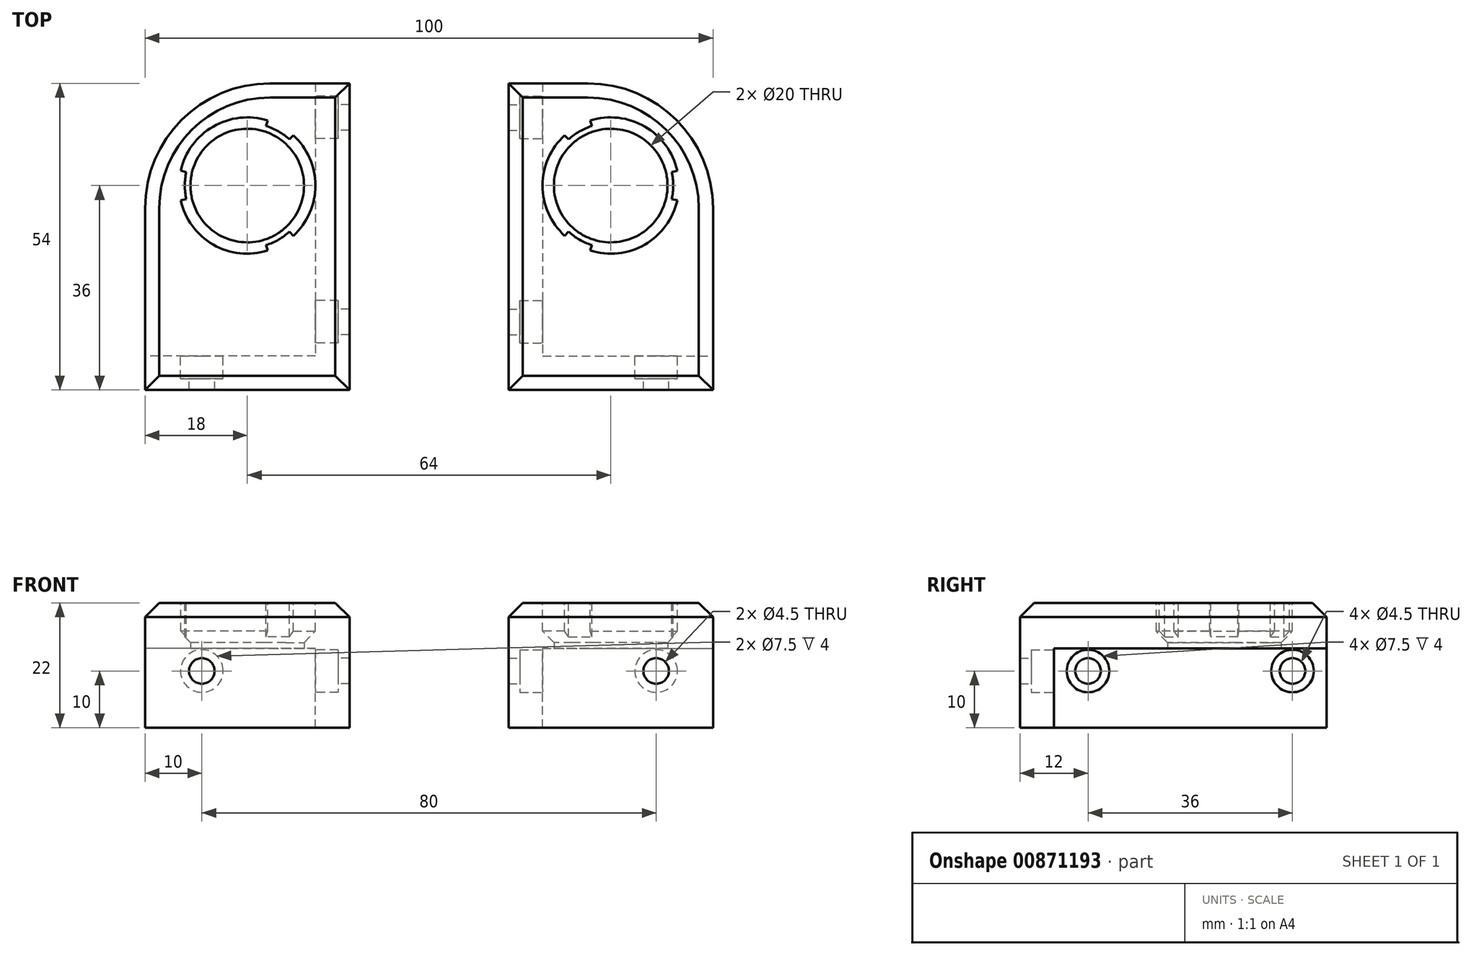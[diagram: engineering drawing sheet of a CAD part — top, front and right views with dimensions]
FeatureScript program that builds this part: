
annotation { "Feature Type Name" : "Feature", "Feature Type Description" : "" }
export const myFeature = defineFeature(function(context is Context, id is Id, definition is map)
    precondition{}
    {
        {
            var Q0;
            Q0=qCreatedBy(makeId("Top.planeOp"),FACE);
            var sketch = newSketch(context, id + "F0", { "sketchPlane" : qUnion([Q0])});
            skLineSegment(sketch, "E0.bottom", {"start": v(0, 0) * mm, "end": v(36, 0) * mm});
            skLineSegment(sketch, "E0.top", {"start": v(0, 54) * mm, "end": v(36, 54) * mm});
            skLineSegment(sketch, "E0.left", {"start": v(0, 0) * mm, "end": v(0, 54) * mm});
            skLineSegment(sketch, "E0.right", {"start": v(36, 0) * mm, "end": v(36, 54) * mm});
            skCircle(sketch, "E1", {"center": v(18, 36) * mm, "radius": 10 * mm});
            skPoint(sketch, "E1.centerSnap0", {"position": v(36, 27) * mm});
            skPoint(sketch, "E1.centerSnap1", {"position": v(18, 54) * mm});
            skSolve(sketch);
        }
        {
            var Q0;
            Q0=qSketchRegion(id+"F0",true);
            extrude(context, id + "F1", {"entities" : qUnion([Q0]), "depth" : 8 * mm, "offsetDistance" : 25 * mm});
        }
        {
            var Q0;
            Q0=makeQuery(id+"F1.opExtrude","CAP_FACE",FACE,{"disambiguationData":[OSD([sQuery(id+"F0.wireOp",EDGE,"E0.bottom"),sQuery(id+"F0.wireOp",EDGE,"E0.top"),sQuery(id+"F0.wireOp",EDGE,"E0.left"),sQuery(id+"F0.wireOp",EDGE,"E0.right"),sQuery(id+"F0.wireOp",EDGE,"E1")])],"isStart":true});
            var sketch = newSketch(context, id + "F2", { "sketchPlane" : qUnion([Q0])});
            skLineSegment(sketch, "E2", {"start": v(0, 0) * mm, "end": v(36, 0) * mm});
            skLineSegment(sketch, "E3", {"start": v(36, 0) * mm, "end": v(36, -54) * mm});
            skLineSegment(sketch, "E4", {"start": v(36, -54) * mm, "end": v(30, -54) * mm});
            skLineSegment(sketch, "E5", {"start": v(30, -54) * mm, "end": v(30, -6) * mm});
            skLineSegment(sketch, "E6", {"start": v(30, -6) * mm, "end": v(0, -6) * mm});
            skLineSegment(sketch, "E7", {"start": v(0, -6) * mm, "end": v(0, 0) * mm});
            skSolve(sketch);
        }
        {
            var Q0;
            Q0=makeQuery(id+"F2.imprint","IMPRINT",FACE,{"disambiguationData":[TD([[makeQuery(id+"F2.imprint","IMPRINT",EDGE,{"derivedFrom":sQuery(id+"F2.wireOp",EDGE,"E2")}),-1.0]])]});
            extrude(context, id + "F3", {"entities" : qUnion([Q0]), "operationType" : NewBodyOperationType.ADD, "depth" : 14 * mm, "offsetDistance" : 25 * mm});
        }
        {
            var Q0;
            Q0=makeQuery(id+"F3.opExtrude","SWEPT_FACE",FACE,{"disambiguationData":[OSD([sQuery(id+"F2.wireOp",EDGE,"E6")])]});
            var sketch = newSketch(context, id + "F4", { "sketchPlane" : qUnion([Q0])});
            skCircle(sketch, "E8", {"center": v(-10, -4) * mm, "radius": 2.25 * mm});
            skSolve(sketch);
        }
        {
            var Q0;
            Q0=qSketchRegion(id+"F4",true);
            extrude(context, id + "F5", {"entities" : qUnion([Q0]), "operationType" : NewBodyOperationType.REMOVE, "endBound" : BoundingType.THROUGH_ALL, "oppositeDirection" : true, "depth" : 25 * mm, "offsetDistance" : 25 * mm});
        }
        {
            var Q0;
            Q0=makeQuery(id+"F3.opExtrude","SWEPT_FACE",FACE,{"disambiguationData":[OSD([sQuery(id+"F2.wireOp",EDGE,"E6")])]});
            var sketch = newSketch(context, id + "F6", { "sketchPlane" : qUnion([Q0])});
            skCircle(sketch, "E9", {"center": v(-10, -4) * mm, "radius": 3.75 * mm});
            skSolve(sketch);
        }
        {
            var Q0;
            Q0=qSketchRegion(id+"F6",true);
            extrude(context, id + "F7", {"entities" : qUnion([Q0]), "operationType" : NewBodyOperationType.REMOVE, "oppositeDirection" : true, "depth" : 4 * mm, "offsetDistance" : 25 * mm});
        }
        {
            var Q0;
            Q0=makeQuery(id+"F3.opExtrude","SWEPT_FACE",FACE,{"disambiguationData":[OSD([sQuery(id+"F2.wireOp",EDGE,"E5")])]});
            var sketch = newSketch(context, id + "F8", { "sketchPlane" : qUnion([Q0])});
            skCircle(sketch, "E10", {"center": v(-48, -4) * mm, "radius": 2.25 * mm});
            skCircle(sketch, "E11", {"center": v(-12, -4) * mm, "radius": 2.25 * mm});
            skSolve(sketch);
        }
        {
            var Q0;
            Q0=qSketchRegion(id+"F8",true);
            extrude(context, id + "F9", {"entities" : qUnion([Q0]), "operationType" : NewBodyOperationType.REMOVE, "endBound" : BoundingType.THROUGH_ALL, "oppositeDirection" : true, "depth" : 25 * mm, "offsetDistance" : 25 * mm});
        }
        {
            var Q0;
            Q0=makeQuery(id+"F3.opExtrude","SWEPT_FACE",FACE,{"disambiguationData":[OSD([sQuery(id+"F2.wireOp",EDGE,"E5")])]});
            var sketch = newSketch(context, id + "F10", { "sketchPlane" : qUnion([Q0])});
            skCircle(sketch, "E12", {"center": v(-48, -4) * mm, "radius": 3.75 * mm});
            skCircle(sketch, "E13", {"center": v(-12, -4) * mm, "radius": 3.75 * mm});
            skSolve(sketch);
        }
        {
            var Q0;
            Q0=qSketchRegion(id+"F10",true);
            extrude(context, id + "F11", {"entities" : qUnion([Q0]), "operationType" : NewBodyOperationType.REMOVE, "oppositeDirection" : true, "depth" : 4 * mm, "offsetDistance" : 25 * mm});
        }
        {
            var Q0;
            Q0=makeQuery(id+"F1.opExtrude","CAP_FACE",FACE,{"disambiguationData":[OSD([sQuery(id+"F0.wireOp",EDGE,"E0.bottom"),sQuery(id+"F0.wireOp",EDGE,"E0.top"),sQuery(id+"F0.wireOp",EDGE,"E0.left"),sQuery(id+"F0.wireOp",EDGE,"E0.right"),sQuery(id+"F0.wireOp",EDGE,"E1")])],"isStart":false});
            var sketch = newSketch(context, id + "F12", { "sketchPlane" : qUnion([Q0])});
            skArc(sketch, "E14", {"start": v(21.6, 47.44) * mm, "mid": v(12, 46.4) * mm, "end": v(6.28, 38.6) * mm});
            skArc(sketch, "E15", {"start": v(7.26, 38.38) * mm, "mid": v(7, 36) * mm, "end": v(7.26, 33.62) * mm});
            skLineSegment(sketch, "E16", {"start": v(7.26, 38.38) * mm, "end": v(6.28, 38.6) * mm});
            skLineSegment(sketch, "E17", {"start": v(7.26, 33.62) * mm, "end": v(6.28, 33.4) * mm});
            skLineSegment(sketch, "E18.1.0", {"start": v(25.43, 27.89) * mm, "end": v(26.1, 27.15) * mm});
            skLineSegment(sketch, "E18.1.1", {"start": v(21.3, 25.5) * mm, "end": v(21.6, 24.56) * mm});
            skLineSegment(sketch, "E18.2.0", {"start": v(21.3, 46.5) * mm, "end": v(21.6, 47.44) * mm});
            skLineSegment(sketch, "E18.2.1", {"start": v(25.43, 44.11) * mm, "end": v(26.1, 44.85) * mm});
            skArc(sketch, "E19.trimOffspring", {"start": v(21.3, 25.5) * mm, "mid": v(23.5, 26.47) * mm, "end": v(25.43, 27.89) * mm});
            skArc(sketch, "E20.trimOffspring", {"start": v(25.43, 44.11) * mm, "mid": v(23.5, 45.53) * mm, "end": v(21.3, 46.5) * mm});
            skArc(sketch, "E21.trimOffspring", {"start": v(26.1, 27.15) * mm, "mid": v(30, 36) * mm, "end": v(26.1, 44.85) * mm});
            skArc(sketch, "E22.trimOffspring", {"start": v(6.28, 33.4) * mm, "mid": v(12, 25.6) * mm, "end": v(21.6, 24.56) * mm});
            skSolve(sketch);
        }
        {
            var Q0;
            Q0=qSketchRegion(id+"F12",true);
            extrude(context, id + "F13", {"entities" : qUnion([Q0]), "operationType" : NewBodyOperationType.REMOVE, "oppositeDirection" : true, "depth" : 7 * mm, "offsetDistance" : 25 * mm});
        }
        {
            var Q0;
            Q0=makeQuery(id+"F1.opExtrude","SWEPT_EDGE",EDGE,{"disambiguationData":[OSD([sQuery(id+"F0.wireOp",EDGE,"E0.top"),sQuery(id+"F0.wireOp",EDGE,"E0.left")])]});
            fillet(context, id + "F14", {"entities" : qUnion([Q0]), "radius" : 22 * mm, "tangentPropagation" : true, "allowEdgeOverflow" : false});
        }
        {
            var Q0;
            Q0=makeQuery(id+"F1.opExtrude","CAP_EDGE",EDGE,{"disambiguationData":[OSD([sQuery(id+"F0.wireOp",EDGE,"E0.right")])],"isStart":false});
            var Q1;
            Q1=makeQuery(id+"F1.opExtrude","CAP_EDGE",EDGE,{"disambiguationData":[OSD([sQuery(id+"F0.wireOp",EDGE,"E0.bottom")])],"isStart":false});
            var Q2;
            Q2=makeQuery(id+"F1.opExtrude","CAP_EDGE",EDGE,{"disambiguationData":[OSD([sQuery(id+"F0.wireOp",EDGE,"E0.top")])],"isStart":false});
            var Q3;
            Q3=makeQuery(id+"F1.opExtrude","CAP_EDGE",EDGE,{"disambiguationData":[OSD([sQuery(id+"F0.wireOp",EDGE,"E0.left")])],"isStart":false});
            chamfer(context, id + "F15", {"entities" : qUnion([Q0, Q1, Q2, Q3]), "width" : 2.5 * mm, "tangentPropagation" : true});
        }
        {
            var Q0;
            Q0=makeQuery(id+"F13.boolean.opBoolean","COPY",EDGE,{"derivedFrom":makeQuery(id+"F13.opExtrude","CAP_EDGE",EDGE,{"disambiguationData":[OSD([sQuery(id+"F12.wireOp",EDGE,"E19.trimOffspring")])],"isStart":false})});
            var Q1;
            Q1=makeQuery(id+"F13.boolean.opBoolean","COPY",EDGE,{"derivedFrom":makeQuery(id+"F13.opExtrude","CAP_EDGE",EDGE,{"disambiguationData":[OSD([sQuery(id+"F12.wireOp",EDGE,"E15")])],"isStart":false})});
            var Q2;
            Q2=makeQuery(id+"F13.boolean.opBoolean","COPY",EDGE,{"derivedFrom":makeQuery(id+"F13.opExtrude","CAP_EDGE",EDGE,{"disambiguationData":[OSD([sQuery(id+"F12.wireOp",EDGE,"E20.trimOffspring")])],"isStart":false})});
            var Q3;
            Q3=makeQuery(id+"F13.boolean.opBoolean","COPY",EDGE,{"derivedFrom":makeQuery(id+"F13.opExtrude","CAP_EDGE",EDGE,{"disambiguationData":[OSD([sQuery(id+"F12.wireOp",EDGE,"E15")])],"isStart":true})});
            var Q4;
            Q4=makeQuery(id+"F13.boolean.opBoolean","COPY",EDGE,{"derivedFrom":makeQuery(id+"F13.opExtrude","CAP_EDGE",EDGE,{"disambiguationData":[OSD([sQuery(id+"F12.wireOp",EDGE,"E20.trimOffspring")])],"isStart":true})});
            var Q5;
            Q5=makeQuery(id+"F13.boolean.opBoolean","COPY",EDGE,{"derivedFrom":makeQuery(id+"F13.opExtrude","CAP_EDGE",EDGE,{"disambiguationData":[OSD([sQuery(id+"F12.wireOp",EDGE,"E19.trimOffspring")])],"isStart":true})});
            chamfer(context, id + "F16", {"entities" : qUnion([Q0, Q1, Q2, Q3, Q4, Q5]), "width" : 1 * mm, "tangentPropagation" : true});
        }
        {
            var Q0;
            Q0=makeQuery(id+"F13.boolean.opBoolean","COPY",EDGE,{"derivedFrom":makeQuery(id+"F13.opExtrude","CAP_EDGE",EDGE,{"disambiguationData":[OSD([sQuery(id+"F12.wireOp",EDGE,"E22.trimOffspring")])],"isStart":false})});
            var Q1;
            Q1=makeQuery(id+"F13.boolean.opBoolean","COPY",EDGE,{"derivedFrom":makeQuery(id+"F13.opExtrude","CAP_EDGE",EDGE,{"disambiguationData":[OSD([sQuery(id+"F12.wireOp",EDGE,"E21.trimOffspring")])],"isStart":false})});
            var Q2;
            Q2=makeQuery(id+"F13.boolean.opBoolean","COPY",EDGE,{"derivedFrom":makeQuery(id+"F13.opExtrude","CAP_EDGE",EDGE,{"disambiguationData":[OSD([sQuery(id+"F12.wireOp",EDGE,"E14")])],"isStart":false})});
            chamfer(context, id + "F17", {"entities" : qUnion([Q0, Q1, Q2]), "width" : 2 * mm, "tangentPropagation" : true});
        }
        {
            var Q0;
            Q0=qCreatedBy(makeId("Right.planeOp"),FACE);
            cPlane(context, id + "F18", {"entities" : qUnion([Q0]), "cplaneType" : CPlaneType.OFFSET, "offset" : 50 * mm, "width" : 150 * mm, "height" : 150 * mm});
        }
        {
            var Q0;
            Q0=makeQuery(id+"F1.opExtrude","SWEPT_BODY",BODY,{"disambiguationData":[OSD([sQuery(id+"F0.wireOp",EDGE,"E0.bottom"),sQuery(id+"F0.wireOp",EDGE,"E0.top"),sQuery(id+"F0.wireOp",EDGE,"E0.left"),sQuery(id+"F0.wireOp",EDGE,"E0.right"),sQuery(id+"F0.wireOp",EDGE,"E1")])]});
            var Q1;
            Q1=qCreatedBy(id+"F18.planeOp",FACE);
            mirror(context, id + "F19", {"operationType" : NewBodyOperationType.ADD, "entities" : qUnion([Q0]), "mirrorPlane" : qUnion([Q1])});
        }
    });
